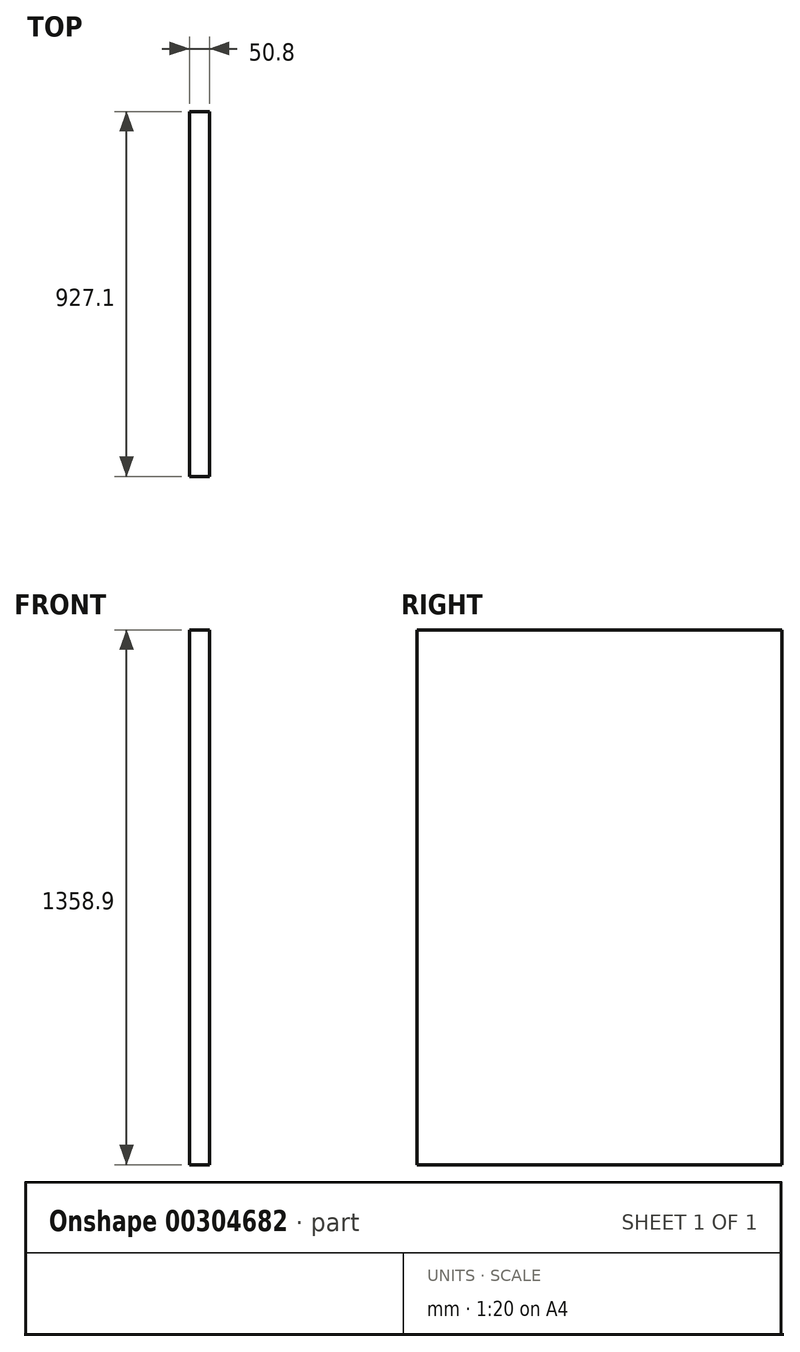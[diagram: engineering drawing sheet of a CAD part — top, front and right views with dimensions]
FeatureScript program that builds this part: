
annotation { "Feature Type Name" : "Feature", "Feature Type Description" : "" }
export const myFeature = defineFeature(function(context is Context, id is Id, definition is map)
    precondition{}
    {
        {
            var Q0;
            Q0=qCreatedBy(makeId("Right.planeOp"),FACE);
            var sketch = newSketch(context, id + "F0", { "sketchPlane" : qUnion([Q0])});
            skLineSegment(sketch, "E0.bottom", {"start": v(-461.22, 777.47) * mm, "end": v(465.88, 777.47) * mm});
            skLineSegment(sketch, "E0.top", {"start": v(-461.22, -581.43) * mm, "end": v(465.88, -581.43) * mm});
            skLineSegment(sketch, "E0.left", {"start": v(-461.22, 777.47) * mm, "end": v(-461.22, -581.43) * mm});
            skLineSegment(sketch, "E0.right", {"start": v(465.88, 777.47) * mm, "end": v(465.88, -581.43) * mm});
            skSolve(sketch);
        }
        {
            var Q0;
            Q0=makeQuery(id+"F0.imprint","IMPRINT",FACE,{"disambiguationData":[TD([[makeQuery(id+"F0.imprint","IMPRINT",EDGE,{"derivedFrom":sQuery(id+"F0.wireOp",EDGE,"E0.bottom")}),-1.0]])]});
            extrude(context, id + "F1", {"entities" : qUnion([Q0]), "depth" : 50.8 * mm});
        }
    });
